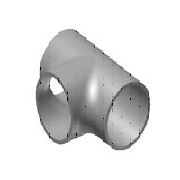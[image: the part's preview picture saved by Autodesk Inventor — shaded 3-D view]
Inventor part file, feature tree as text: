
AUTODESK INVENTOR PART (.ipt)
format: ipt  version: 2023.2 (Build 272271030, 271C)  size: 214,016 bytes
history: native  units: mm
features: other x6, extrude x4, sketch x4, fillet x2
ambient origin geometry x8: Origin, YZ Plane, XZ Plane, XY Plane, X Axis, Y Axis, Z Axis, Center Point
bodies: Solid1 (feature_tree)
feature tree (16):
  extrude  "Extrusion1"  Depth=200.0mm
  extrude  "Extrusion2"  Depth=108.0mm
  fillet  "Fillet1"  Radius=80.0mm
  extrude  "Extrusion3"  Depth=20.0mm
  extrude  "Extrusion4"  Depth=80.0mm
  fillet  "Fillet2"  [1 undecoded]
  other  "Work Point1"
  other  "Work Point2"
  other  "Work Point3"
  other  "Work Axis1"
  other  "Work Axis2"
  other  "Work Axis3"
  sketch  "Sketch1"  dims[d0=108.0mm d2=200.0mm]
  sketch  "Sketch2"  dims[d3=0.0mm d4=108.0mm d6=80.0mm]
  sketch  "Sketch3"  dims[d7=0.0mm d8=20.0mm]
  sketch  "Sketch4"  dims[d9=92.0mm d10=80.0mm d11=0.0mm d12=92.0mm d13=80.0mm d14=0.0mm d15=28.0mm]
note: 1 required parameter value undecoded (feature->parameter linkage not recoverable at this tier; creation-order binding heuristic only, values carry confidence <= 0.55)
